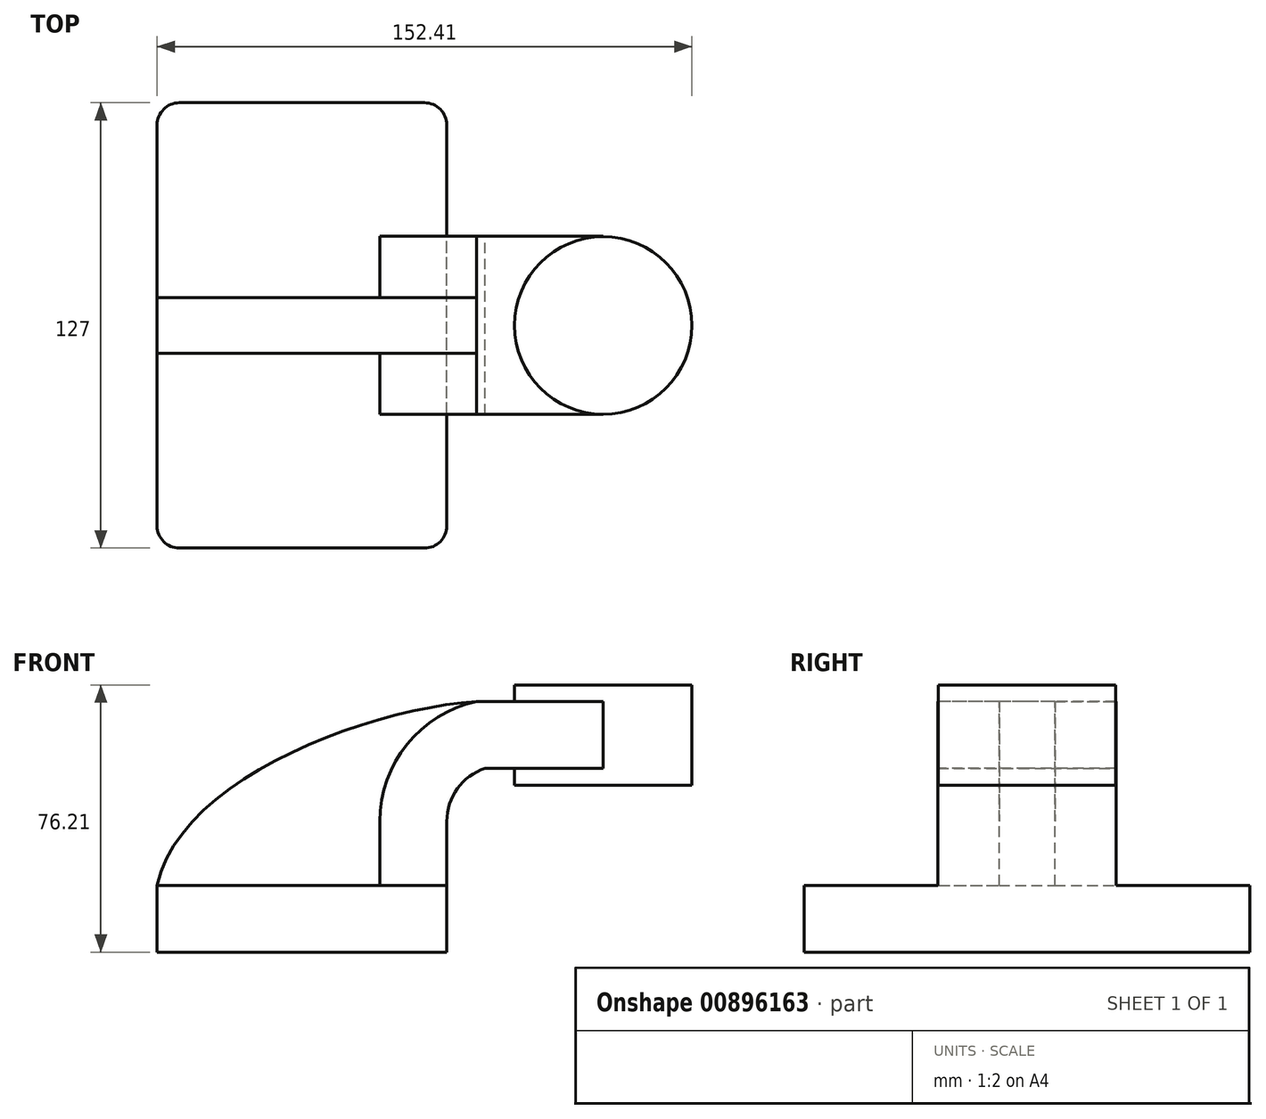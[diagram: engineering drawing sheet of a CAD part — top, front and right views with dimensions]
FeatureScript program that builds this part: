
annotation { "Feature Type Name" : "Feature", "Feature Type Description" : "" }
export const myFeature = defineFeature(function(context is Context, id is Id, definition is map)
    precondition{}
    {
        {
            var Q0;
            Q0=qCreatedBy(makeId("Front.planeOp"),FACE);
            var sketch = newSketch(context, id + "F0", { "sketchPlane" : qUnion([Q0])});
            skLineSegment(sketch, "E0.bottom", {"start": v(-41.28, 9.52) * mm, "end": v(41.28, 9.53) * mm});
            skLineSegment(sketch, "E0.top", {"start": v(-41.28, -9.53) * mm, "end": v(41.28, -9.53) * mm});
            skLineSegment(sketch, "E0.left", {"start": v(-41.28, 9.52) * mm, "end": v(-41.28, -9.53) * mm});
            skLineSegment(sketch, "E0.right", {"start": v(41.28, 9.53) * mm, "end": v(41.28, -9.52) * mm});
            skPoint(sketch, "E0.middle", {"position": v(0, 0) * mm});
            skLineSegment(sketch, "E1.bottom", {"start": v(60.32, 66.68) * mm, "end": v(111.12, 66.68) * mm});
            skLineSegment(sketch, "E1.top", {"start": v(60.32, 38.1) * mm, "end": v(111.12, 38.1) * mm});
            skLineSegment(sketch, "E1.left", {"start": v(60.32, 66.68) * mm, "end": v(60.32, 38.1) * mm});
            skLineSegment(sketch, "E1.right", {"start": v(111.12, 66.68) * mm, "end": v(111.12, 38.1) * mm});
            skPoint(sketch, "E1.middle", {"position": v(85.72, 52.39) * mm});
            skPoint(sketch, "E2.middle", {"position": v(41.28, 9.53) * mm});
            skLineSegment(sketch, "E3", {"start": v(41.27, 9.53) * mm, "end": v(41.27, 27.8) * mm});
            skArc(sketch, "E4", {"start": v(41.27, 27.8) * mm, "mid": v(44.29, 37.1) * mm, "end": v(52.18, 42.88) * mm});
            skLineSegment(sketch, "E5", {"start": v(52.18, 42.88) * mm, "end": v(85.83, 42.88) * mm});
            skLineSegment(sketch, "E6.0", {"start": v(49.72, 61.93) * mm, "end": v(85.83, 61.93) * mm});
            skArc(sketch, "E6.1", {"start": v(22.23, 27.8) * mm, "mid": v(29.95, 49.71) * mm, "end": v(49.72, 61.93) * mm});
            skLineSegment(sketch, "E6.2", {"start": v(22.23, 9.53) * mm, "end": v(22.23, 27.8) * mm});
            skLineSegment(sketch, "E7", {"start": v(85.83, 38.1) * mm, "end": v(85.83, 66.68) * mm});
            skFitSpline(sketch, "E8", {"points": [v(-41.28, 9.52) * mm, v(49.72, 61.92) * mm], "startDerivative": vector(18.63, 90.1) * mm, "endDerivative": vector(94.84, 6.25) * mm});
            skSolve(sketch);
        }
        {
            var Q0;
            Q0=makeQuery(id+"F0.imprint","IMPRINT",FACE,{"disambiguationData":[TD([[makeQuery(id+"F0.imprint","IMPRINT",EDGE,{"derivedFrom":sQuery(id+"F0.wireOp",EDGE,"E0.top")}),1.0]])]});
            extrude(context, id + "F1", {"entities" : qUnion([Q0]), "endBound" : BoundingType.SYMMETRIC, "depth" : 127 * mm, "offsetDistance" : 25.4 * mm});
        }
        {
            var Q0;
            {var subQ1=sQuery(id+"F0.wireOp",EDGE,"E3");Q0=makeQuery(id+"F0.imprint","IMPRINT",FACE,{"disambiguationData":[TD([[makeQuery(id+"F0.imprint","IMPRINT",EDGE,{"derivedFrom":subQ1}),1.0]])]});}
            var Q1;
            {var subQ0=sQuery(id+"F0.wireOp",EDGE,"E6.0");var subQ1=sQuery(id+"F0.wireOp",EDGE,"E1.left");var subQ2=makeQuery(id+"F0.imprint","INTERSECT",VERTEX,{"derivedFrom":[subQ1,subQ0]});Q1=makeQuery(id+"F0.imprint","IMPRINT",FACE,{"disambiguationData":[TD([[makeQuery(id+"F0.imprint","IMPRINT",EDGE,{"disambiguationData":[TD([[subQ2,-1.0]])],"derivedFrom":subQ1}),1.0]])]});}
            extrude(context, id + "F2", {"entities" : qUnion([Q0, Q1]), "operationType" : NewBodyOperationType.ADD, "endBound" : BoundingType.SYMMETRIC, "depth" : 50.8 * mm, "offsetDistance" : 25.4 * mm});
        }
        {
            var Q0;
            {var subQ3=sQuery(id+"F0.wireOp",EDGE,"E6.2");Q0=makeQuery(id+"F0.imprint","IMPRINT",FACE,{"disambiguationData":[TD([[makeQuery(id+"F0.imprint","IMPRINT",EDGE,{"derivedFrom":subQ3}),1.0]])]});}
            extrude(context, id + "F3", {"entities" : qUnion([Q0]), "operationType" : NewBodyOperationType.ADD, "endBound" : BoundingType.SYMMETRIC, "depth" : 15.88 * mm, "offsetDistance" : 25.4 * mm});
        }
        {
            var Q0;
            {var subQ4=sQuery(id+"F0.wireOp",EDGE,"E1.right");Q0=makeQuery(id+"F0.imprint","IMPRINT",FACE,{"disambiguationData":[TD([[makeQuery(id+"F0.imprint","IMPRINT",EDGE,{"derivedFrom":subQ4}),-1.0]])]});}
            var Q1;
            Q1=sQuery(id+"F0.wireOp",EDGE,"E7");
            revolve(context, id + "F4", {"operationType" : NewBodyOperationType.ADD, "surfaceOperationType" : NewSurfaceOperationType.NEW, "entities" : qUnion([Q0]), "axis" : qUnion([Q1]), "revolveType" : RevolveType.FULL});
        }
        {
            var Q0;
            Q0=makeQuery(id+"F1.opExtrude","CAP_EDGE",EDGE,{"disambiguationData":[OSD([sQuery(id+"F0.wireOp",EDGE,"E0.right")])],"isStart":true});
            var Q1;
            Q1=makeQuery(id+"F1.opExtrude","CAP_EDGE",EDGE,{"disambiguationData":[OSD([sQuery(id+"F0.wireOp",EDGE,"E0.left")])],"isStart":true});
            var Q2;
            Q2=makeQuery(id+"F1.opExtrude","CAP_EDGE",EDGE,{"disambiguationData":[OSD([sQuery(id+"F0.wireOp",EDGE,"E0.left")])],"isStart":false});
            var Q3;
            Q3=makeQuery(id+"F1.opExtrude","CAP_EDGE",EDGE,{"disambiguationData":[OSD([sQuery(id+"F0.wireOp",EDGE,"E0.right")])],"isStart":false});
            fillet(context, id + "F5", {"entities" : qUnion([Q0, Q1, Q2, Q3]), "radius" : 6.35 * mm, "tangentPropagation" : true, "allowEdgeOverflow" : false});
        }
    });
